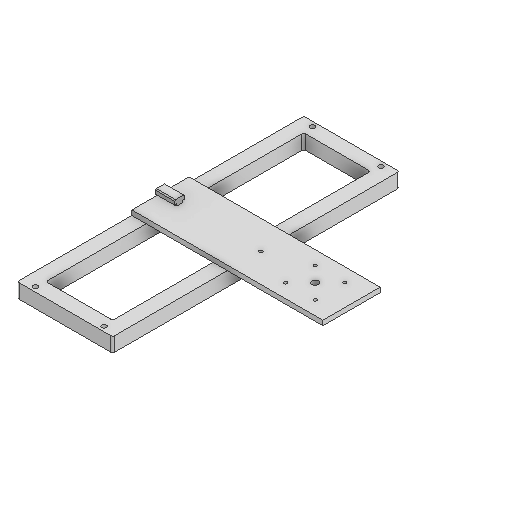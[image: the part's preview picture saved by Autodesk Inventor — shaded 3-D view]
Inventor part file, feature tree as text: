
AUTODESK INVENTOR PART (.ipt)
format: ipt  version: 2025.1 (Build 291241000, 241)  size: 204,800 bytes
history: native  units: mm
features: sketch x8, extrude x4, hole x4, other x1, fillet x1
ambient origin geometry x8: Origin, YZ Plane, XZ Plane, XY Plane, X Axis, Y Axis, Z Axis, Center Point
bodies: Body1 (feature_tree)
feature tree (18):
  other  "Bryła1"
  sketch  "Szkic1"
  sketch  "Szkic2"
  extrude  "Wyciągnięcie proste1"  Depth=300.0mm
  extrude  "Wyciągnięcie proste2"  Depth=100.0mm
  fillet  "Zaokrąglenie1"  Radius=70.0mm
  hole  "Otwór1"  [1 undecoded]
  extrude  "Wyciągnięcie proste3"  Depth=15.0mm
  extrude  "Wyciągnięcie proste4"  Depth=15.0mm
  hole  "Otwór2"  [1 undecoded]
  hole  "Otwór3"  [1 undecoded]
  hole  "Otwór4"  [1 undecoded]
  sketch  "Szkic3"
  sketch  "Szkic4"
  sketch  "Szkic5"
  sketch  "Szkic6"
  sketch  "Szkic7"
  sketch  "Szkic8"
note: 4 required parameter values undecoded (feature->parameter linkage not recoverable at this tier; creation-order binding heuristic only, values carry confidence <= 0.55)
